# Revit family: 706530001_Silla Plegable Ducha
name_source: partatom
category: Plumbing Fixtures
units: mm (PartAtom-declared; Revit-internal decimal feet)

## family parameters
Always vertical = Yes
Cut with Voids When Loaded = No
Host = Wall
OmniClass Number = 23.31.17.23
OmniClass Title = Shower Seats
Part Type = Normal
Room Calculation Point = No
Round Connector Dimension = Use Diameter
Shared = No

## types (1)
- Type 1
    Alto = 201 mm
    Ancho = 438 mm
    Creado por = BIMBAU
    Default Elevation = 0 mm  [stored 0 ft]
    Description = Un elemento para el apoyo, seguridad y protección para los usuarios; además, sobrepasa la prueba de carga exigida por norma de 150kg y con aguante por encima de 300kg
    Fecha de creación = 15/04/2021
    Garantía = 1 Año
    Manufacturer = Corona
    Material = Corona_Acero inoxidable
    Material 2 = Corona_Plastico_Blanco
    Model = Silla Plegable
    Profundidad = 360 mm
    Referencia = 706530001
    URL = https://corona.co
    Uso = Institucional

note: [stored X ft] marks values corroborated as IEEE doubles in the binary element streams (Revit-internal decimal feet)

## geometry (parser evidence)
native form markers: Sweep x6
no freeform markers — native parametric forms only
